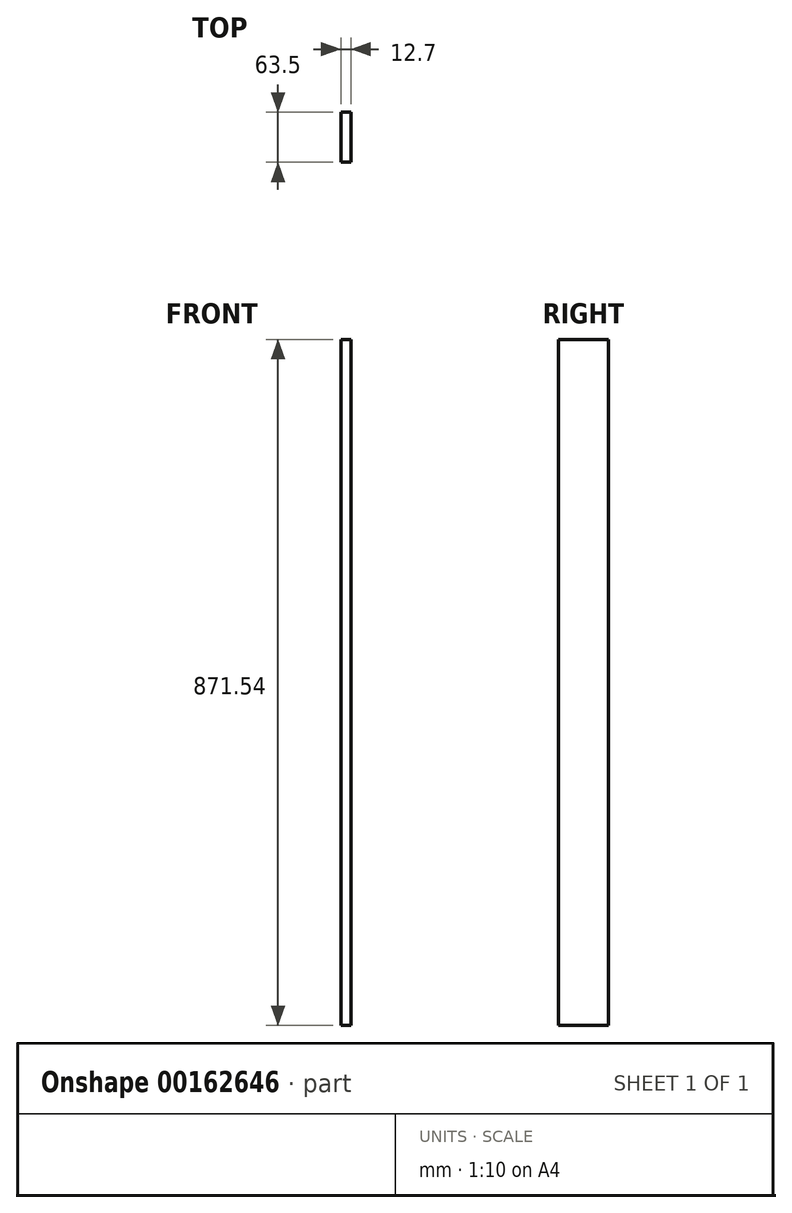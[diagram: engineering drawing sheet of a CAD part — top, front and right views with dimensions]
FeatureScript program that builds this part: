
annotation { "Feature Type Name" : "Feature", "Feature Type Description" : "" }
export const myFeature = defineFeature(function(context is Context, id is Id, definition is map)
    precondition{}
    {
        {
            var Q0;
            Q0=qCreatedBy(makeId("Right.planeOp"),FACE);
            var sketch = newSketch(context, id + "F0", { "sketchPlane" : qUnion([Q0])});
            skLineSegment(sketch, "E0.bottom", {"start": v(-77.28, 650.6) * mm, "end": v(-13.78, 650.6) * mm});
            skLineSegment(sketch, "E0.top", {"start": v(-77.28, -220.94) * mm, "end": v(-13.78, -220.94) * mm});
            skLineSegment(sketch, "E0.left", {"start": v(-77.28, 650.6) * mm, "end": v(-77.28, -220.94) * mm});
            skLineSegment(sketch, "E0.right", {"start": v(-13.78, 650.6) * mm, "end": v(-13.78, -220.94) * mm});
            skSolve(sketch);
        }
        {
            var Q0;
            Q0 = qSketchRegion(id + "F0", true);
            extrude(context, id + "F1", {"entities" : qUnion([Q0]), "depth" : 12.7 * mm});
        }
    });
